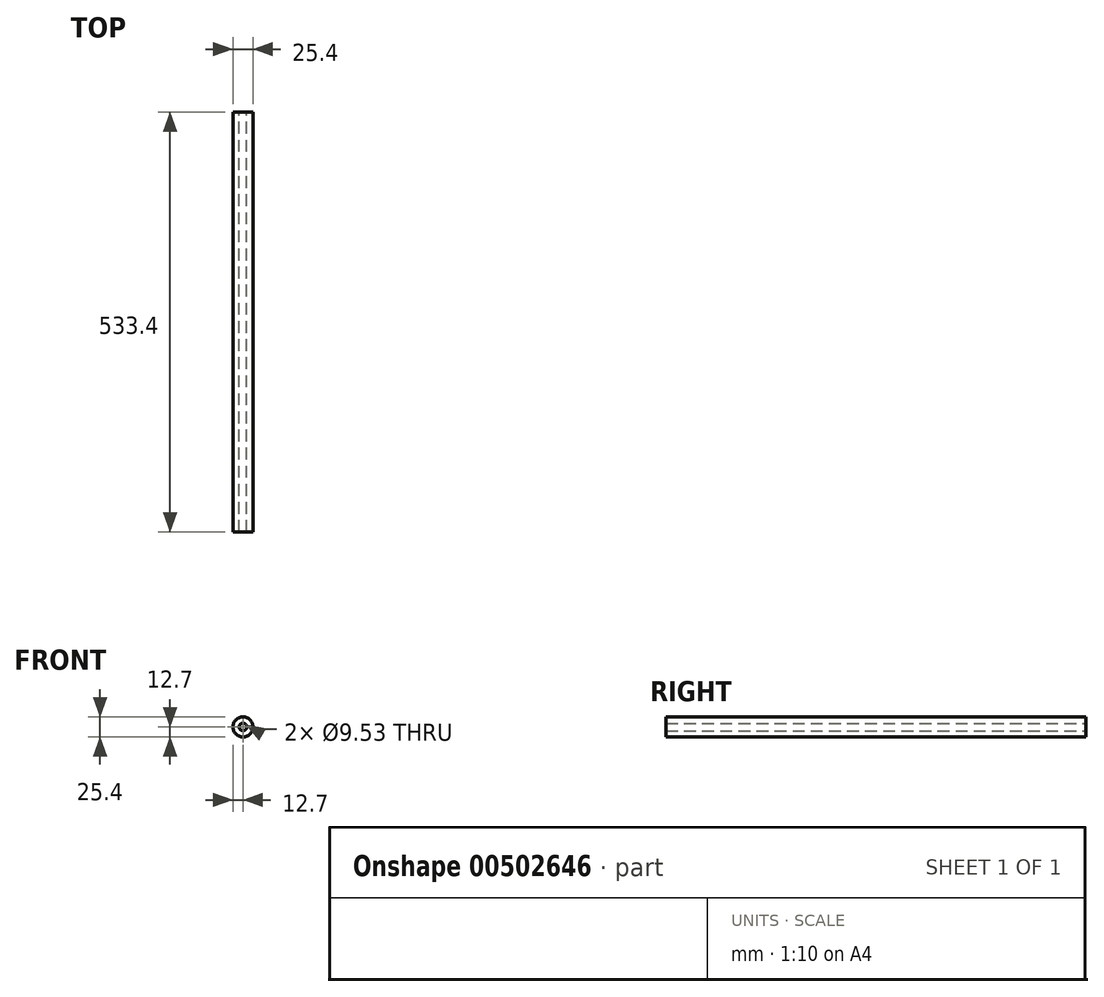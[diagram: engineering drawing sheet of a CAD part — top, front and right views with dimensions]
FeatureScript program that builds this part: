
annotation { "Feature Type Name" : "Feature", "Feature Type Description" : "" }
export const myFeature = defineFeature(function(context is Context, id is Id, definition is map)
    precondition{}
    {
        {
            var Q0;
            Q0=qCreatedBy(makeId("Front.planeOp"),FACE);
            var sketch = newSketch(context, id + "F0", { "sketchPlane" : qUnion([Q0])});
            skCircle(sketch, "E0", {"center": v(0, 0) * mm, "radius": 12.7 * mm});
            skCircle(sketch, "E1", {"center": v(0, 0) * mm, "radius": 4.76 * mm});
            skSolve(sketch);
        }
        {
            var Q0;
            Q0=makeQuery(id+"F0.imprint","IMPRINT",FACE,{"disambiguationData":[TD([[makeQuery(id+"F0.imprint","IMPRINT",EDGE,{"derivedFrom":sQuery(id+"F0.wireOp",EDGE,"E0")}),1.0]])]});
            extrude(context, id + "F1", {"entities" : qUnion([Q0]), "depth" : 533.4 * mm});
        }
    });
